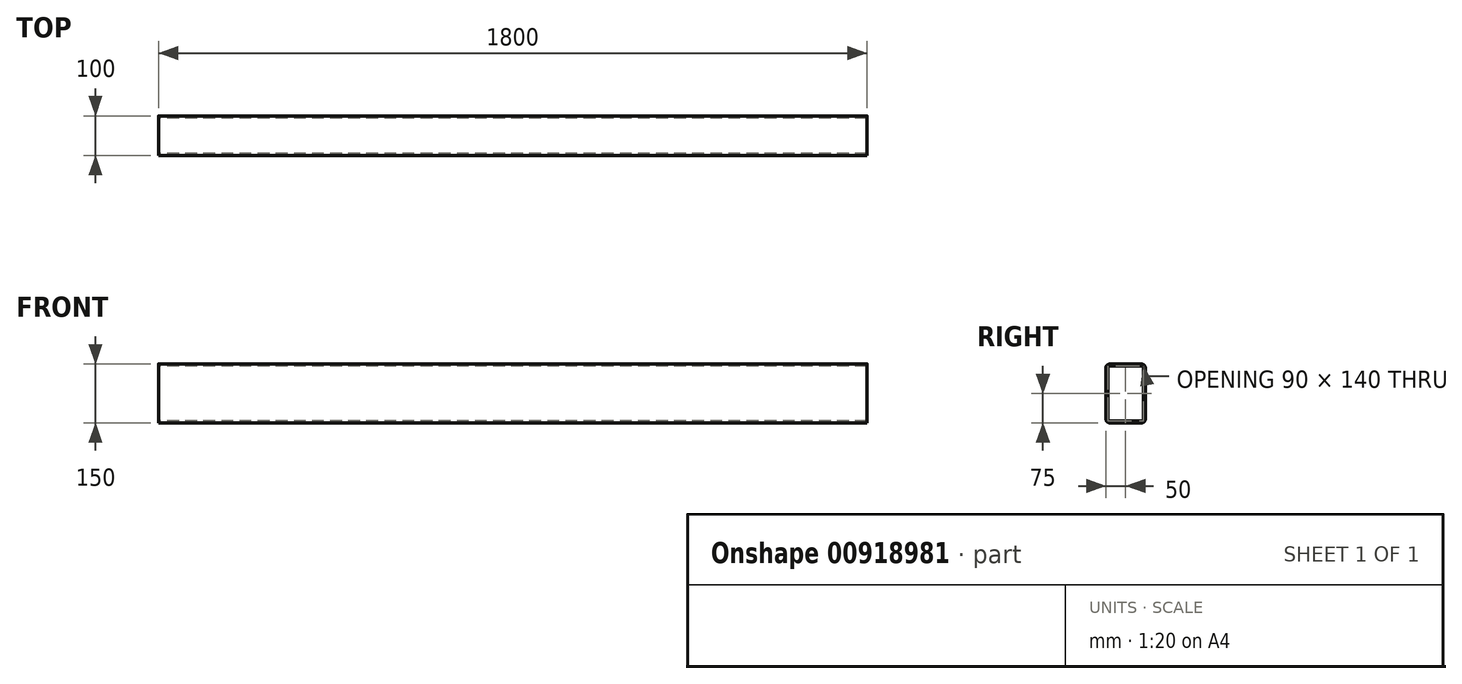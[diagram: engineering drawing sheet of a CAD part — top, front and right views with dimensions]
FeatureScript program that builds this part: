
annotation { "Feature Type Name" : "Feature", "Feature Type Description" : "" }
export const myFeature = defineFeature(function(context is Context, id is Id, definition is map)
    precondition{}
    {
        {
            var Q0;
            Q0=qCreatedBy(makeId("Right.planeOp"),FACE);
            var sketch = newSketch(context, id + "F0", { "sketchPlane" : qUnion([Q0])});
            skLineSegment(sketch, "E0.bottom", {"start": v(40, 75) * mm, "end": v(-40, 75) * mm});
            skLineSegment(sketch, "E0.top", {"start": v(40, -75) * mm, "end": v(-40, -75) * mm});
            skLineSegment(sketch, "E0.left", {"start": v(50, 65) * mm, "end": v(50, -65) * mm});
            skLineSegment(sketch, "E0.right", {"start": v(-50, 65) * mm, "end": v(-50, -65) * mm});
            skPoint(sketch, "E0.middle", {"position": v(0, 0) * mm});
            skPoint(sketch, "E1.visualSharp", {"position": v(-50, 75) * mm});
            skArc(sketch, "E1.filletArc", {"start": v(-40, 75) * mm, "mid": v(-47.07, 72.07) * mm, "end": v(-50, 65) * mm});
            skPoint(sketch, "E2.visualSharp", {"position": v(50, 75) * mm});
            skArc(sketch, "E2.filletArc", {"start": v(50, 65) * mm, "mid": v(47.07, 72.07) * mm, "end": v(40, 75) * mm});
            skPoint(sketch, "E3.visualSharp", {"position": v(50, -75) * mm});
            skArc(sketch, "E3.filletArc", {"start": v(40, -75) * mm, "mid": v(47.07, -72.07) * mm, "end": v(50, -65) * mm});
            skPoint(sketch, "E4.visualSharp", {"position": v(-50, -75) * mm});
            skArc(sketch, "E4.filletArc", {"start": v(-50, -65) * mm, "mid": v(-47.07, -72.07) * mm, "end": v(-40, -75) * mm});
            skLineSegment(sketch, "E5.0", {"start": v(45, 65) * mm, "end": v(45, -65) * mm});
            skLineSegment(sketch, "E6.0", {"start": v(40, -70) * mm, "end": v(-40, -70) * mm});
            skLineSegment(sketch, "E7.0", {"start": v(-45, 65) * mm, "end": v(-45, -65) * mm});
            skLineSegment(sketch, "E8.0", {"start": v(40, 70) * mm, "end": v(-40, 70) * mm});
            skArc(sketch, "E9.0", {"start": v(40, -70) * mm, "mid": v(43.54, -68.54) * mm, "end": v(45, -65) * mm});
            skArc(sketch, "E10.0", {"start": v(-45, -65) * mm, "mid": v(-43.54, -68.54) * mm, "end": v(-40, -70) * mm});
            skArc(sketch, "E11.0", {"start": v(-40, 70) * mm, "mid": v(-43.54, 68.54) * mm, "end": v(-45, 65) * mm});
            skArc(sketch, "E12.0", {"start": v(45, 65) * mm, "mid": v(43.54, 68.54) * mm, "end": v(40, 70) * mm});
            skSolve(sketch);
        }
        {
            var Q0;
            Q0=makeQuery(id+"F0.imprint","IMPRINT",FACE,{"disambiguationData":[TD([[makeQuery(id+"F0.imprint","IMPRINT",EDGE,{"derivedFrom":sQuery(id+"F0.wireOp",EDGE,"E0.bottom")}),1.0]])]});
            extrude(context, id + "F1", {"entities" : qUnion([Q0]), "depth" : 1800 * mm, "offsetDistance" : 25 * mm});
        }
    });
